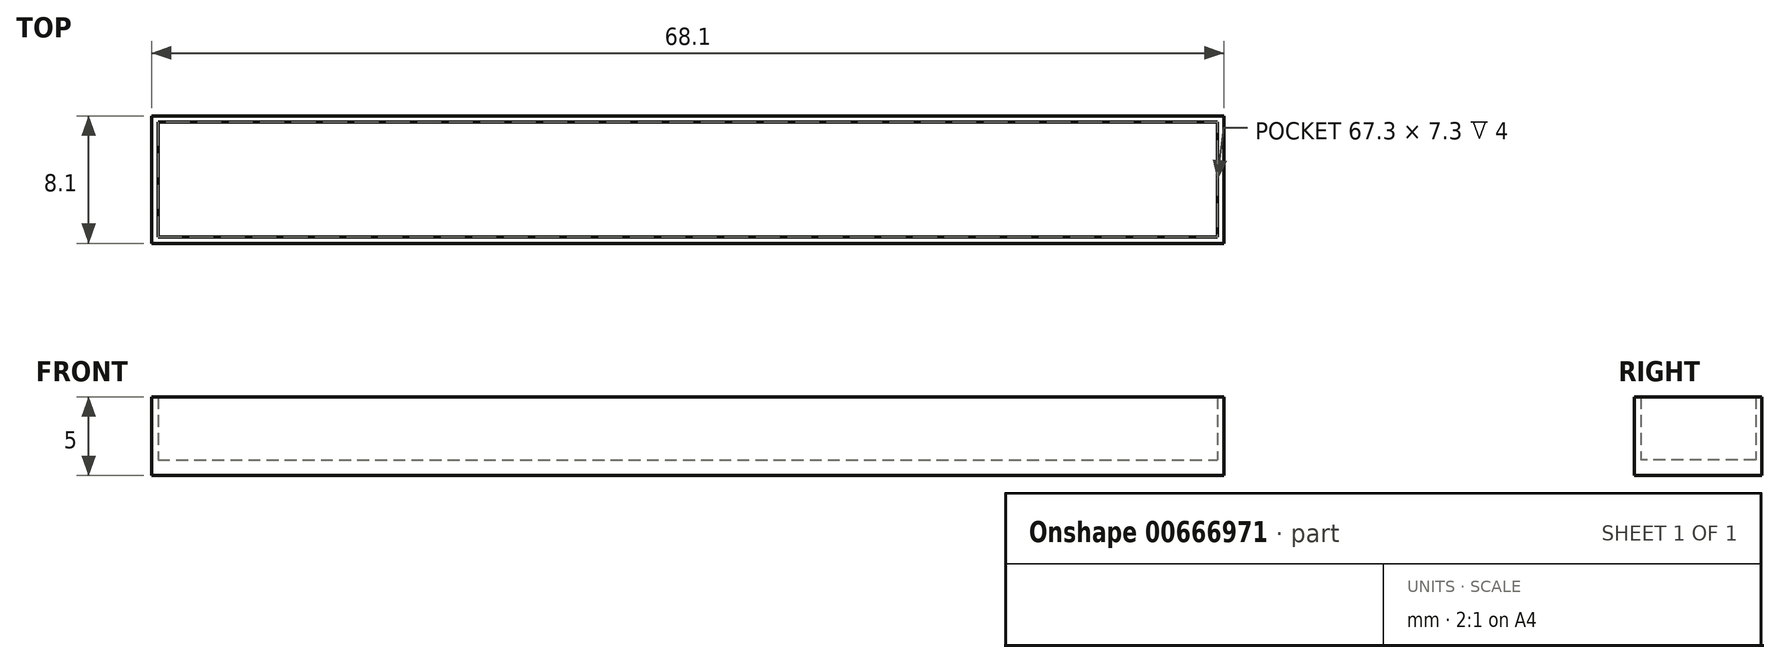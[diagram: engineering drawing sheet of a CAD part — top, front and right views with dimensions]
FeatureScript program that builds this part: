
annotation { "Feature Type Name" : "Feature", "Feature Type Description" : "" }
export const myFeature = defineFeature(function(context is Context, id is Id, definition is map)
    precondition{}
    {
        {
            var Q0;
            Q0=qCreatedBy(makeId("Top.planeOp"),FACE);
            var sketch = newSketch(context, id + "F0", { "sketchPlane" : qUnion([Q0])});
            skLineSegment(sketch, "E0", {"start": v(0, 0) * mm, "end": v(0, 8.1) * mm});
            skLineSegment(sketch, "E1", {"start": v(0, 0) * mm, "end": v(68.1, 0) * mm});
            skLineSegment(sketch, "E2", {"start": v(68.1, 0) * mm, "end": v(68.1, 8.1) * mm});
            skLineSegment(sketch, "E3", {"start": v(68.1, 8.1) * mm, "end": v(0, 8.1) * mm});
            skLineSegment(sketch, "E4", {"start": v(0.4, 7.7) * mm, "end": v(0.4, 0.4) * mm});
            skLineSegment(sketch, "E5", {"start": v(0.4, 7.7) * mm, "end": v(67.7, 7.7) * mm});
            skLineSegment(sketch, "E6", {"start": v(67.7, 7.7) * mm, "end": v(67.7, 0.4) * mm});
            skLineSegment(sketch, "E7", {"start": v(67.7, 0.4) * mm, "end": v(0.4, 0.4) * mm});
            skSolve(sketch);
        }
        {
            var Q0;
            Q0=makeQuery(id+"F0.imprint","IMPRINT",FACE,{"disambiguationData":[TD([[makeQuery(id+"F0.imprint","IMPRINT",EDGE,{"derivedFrom":sQuery(id+"F0.wireOp",EDGE,"E0")}),-1.0]])]});
            extrude(context, id + "F1", {"entities" : qUnion([Q0]), "depth" : 5 * mm, "offsetDistance" : 25 * mm});
        }
        {
            var Q0;
            Q0 = qSketchRegion(id + "F0", true);
            var Q1;
            Q1=makeQuery(id+"F0.imprint","IMPRINT",FACE,{"disambiguationData":[TD([[makeQuery(id+"F0.imprint","IMPRINT",EDGE,{"derivedFrom":sQuery(id+"F0.wireOp",EDGE,"E4")}),1.0]])]});
            extrude(context, id + "F2", {"entities" : qUnion([Q0, Q1]), "operationType" : NewBodyOperationType.ADD, "depth" : 1 * mm, "offsetDistance" : 25 * mm});
        }
    });
